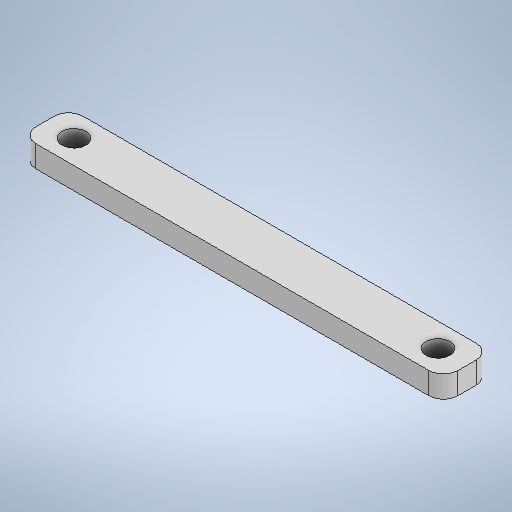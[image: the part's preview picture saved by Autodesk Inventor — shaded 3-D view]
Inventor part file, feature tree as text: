
AUTODESK INVENTOR PART (.ipt)
format: ipt  version: 2025.1 (Build 291241020, 241B)  size: 729,088 bytes
history: native  units: in
note: dims shown in document units (in); Inventor stores cm internally (conversion verified against a paired STEP export)
features: extrude x15, sketch x15, other x3, fillet x3, pattern_circular x1, plane x1, split x1
ambient origin geometry x8: Origin, YZ Plane, XZ Plane, XY Plane, X Axis, Y Axis, Z Axis, Center Point
bodies: Solid1 (feature_tree)
feature tree (39):
  other  "servoMoldAssembly.iam"
  other  "block.ipt:1"
  other  "sg90horn.ipt:1"
  extrude  "Extrusion1"  Depth=0.3937in TaperAngle=0.0deg
  extrude  "Extrusion2"  Depth=0.3937in TaperAngle=0.0deg
  extrude  "Extrusion3"  Depth=0.0591in TaperAngle=0.0deg
  extrude  "Extrusion4"  Depth=0.0591in TaperAngle=0.0deg
  extrude  "Extrusion5"  Depth=1.9685in
  extrude  "Extrusion6"  Depth=0.3937in TaperAngle=0.0deg
  extrude  "Extrusion7"  Depth=0.3937in TaperAngle=0.0deg
  extrude  "Extrusion8"  Depth=0.1299in
  extrude  "Extrusion10"  Depth=0.0787in TaperAngle=0.0deg
  extrude  "Extrusion11"  Depth=0.0787in TaperAngle=0.0deg
  fillet  "Fillet1"  Radius=0.0787in
  extrude  "Extrusion12"  Depth=0.8268in
  fillet  "Fillet2"  Radius=1.1934in
  extrude  "Extrusion13"  TaperAngle=90.0deg  [1 undecoded]
  pattern_circular  "Circular Pattern2"  Count=20 Angle=240.0deg
  extrude  "Extrusion14"  Depth=0.3937in
  extrude  "Extrusion15"  Depth=0.0787in
  extrude  "Extrusion16"  Depth=0.3937in TaperAngle=0.0deg
  fillet  "Fillet3"  Radius=0.0787in
  plane  "Work Plane1"
  split  "Split1"
  sketch  "Sketch3"  dims[d0=0.3937in d1=0.3937in d2=0.0in]
  sketch  "Sketch4"  dims[d3=0.2795in d4=0.3937in d5=0.0in]
  sketch  "Sketch5"  dims[d6=0.0591in d7=0.0in d8=0.0591in d9=0.0in]
  sketch  "Sketch6"  dims[d10=0.0591in d11=0.0in d12=0.0591in d13=0.0in]
  sketch  "Sketch7"  dims[d14=1.4173in d15=1.9685in]
  sketch  "Sketch8"  dims[d16=0.0in d17=0.3937in d18=0.0in]
  sketch  "Sketch9"  dims[d19=0.3937in d20=0.0in d29=0.2362in d30=0.0in]
  sketch  "Sketch10"  dims[d31=0.2362in d32=0.1299in]
  sketch  "Sketch12"  dims[d33=0.0787in d34=0.2362in d35=0.0in]
  sketch  "Sketch13"  dims[d36=0.0787in d37=0.2362in d38=0.0in d39=0.0787in]
  sketch  "Sketch14"  dims[d40=0.0984in d41=0.8268in d42=1.1934in]
  sketch  "Sketch15"  dims[d43=0.0591in d44=90.0deg]
  sketch  "Sketch16"  dims[d45=0.3937in d46=0.0in d47=7.874in d48=240.0deg]
  sketch  "Sketch17"  dims[d50=0.3937in d51=0.0in d52=0.1299in]
  sketch  "Sketch18"  dims[d53=0.3937in d54=0.0in d55=0.1575in d56=0.3937in d57=0.0in d58=0.0787in d59=-0.0591in]
note: 1 required parameter value undecoded (feature->parameter linkage not recoverable at this tier; creation-order binding heuristic only, values carry confidence <= 0.55)
